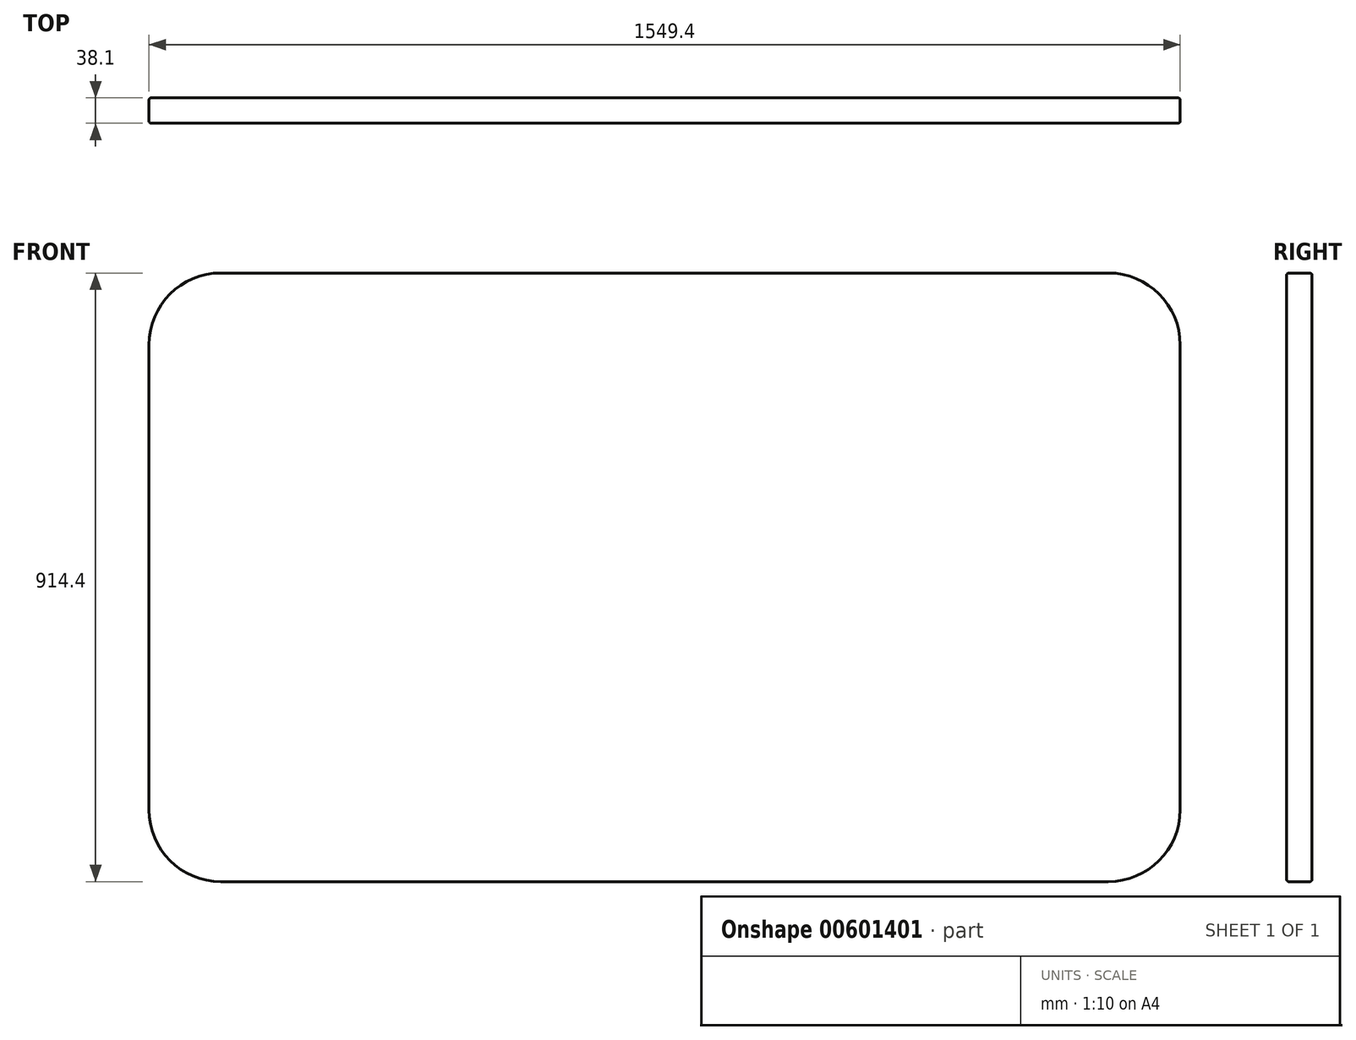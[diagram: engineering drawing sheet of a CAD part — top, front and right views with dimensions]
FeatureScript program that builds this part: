
annotation { "Feature Type Name" : "Feature", "Feature Type Description" : "" }
export const myFeature = defineFeature(function(context is Context, id is Id, definition is map)
    precondition{}
    {
        {
            var Q0;
            Q0=qCreatedBy(makeId("Front.planeOp"),FACE);
            var sketch = newSketch(context, id + "F0", { "sketchPlane" : qUnion([Q0])});
            skLineSegment(sketch, "E0.bottom", {"start": v(-666.75, 457.2) * mm, "end": v(666.75, 457.2) * mm});
            skLineSegment(sketch, "E0.top", {"start": v(-666.75, -457.2) * mm, "end": v(666.75, -457.2) * mm});
            skLineSegment(sketch, "E0.left", {"start": v(-774.7, 349.25) * mm, "end": v(-774.7, -349.25) * mm});
            skLineSegment(sketch, "E0.right", {"start": v(774.7, 349.25) * mm, "end": v(774.7, -349.25) * mm});
            skPoint(sketch, "E0.middle", {"position": v(0, 0) * mm});
            skPoint(sketch, "E1.visualSharp", {"position": v(774.7, 457.2) * mm});
            skArc(sketch, "E1.filletArc", {"start": v(774.7, 349.25) * mm, "mid": v(743.08, 425.58) * mm, "end": v(666.75, 457.2) * mm});
            skPoint(sketch, "E2.visualSharp", {"position": v(774.7, -457.2) * mm});
            skArc(sketch, "E2.filletArc", {"start": v(666.75, -457.2) * mm, "mid": v(743.08, -425.58) * mm, "end": v(774.7, -349.25) * mm});
            skPoint(sketch, "E3.visualSharp", {"position": v(-774.7, -457.2) * mm});
            skArc(sketch, "E3.filletArc", {"start": v(-774.7, -349.25) * mm, "mid": v(-743.08, -425.58) * mm, "end": v(-666.75, -457.2) * mm});
            skPoint(sketch, "E4.visualSharp", {"position": v(-774.7, 457.2) * mm});
            skArc(sketch, "E4.filletArc", {"start": v(-666.75, 457.2) * mm, "mid": v(-743.08, 425.58) * mm, "end": v(-774.7, 349.25) * mm});
            skSolve(sketch);
        }
        {
            var Q0;
            Q0 = qSketchRegion(id + "F0", true);
            extrude(context, id + "F1", {"entities" : qUnion([Q0]), "endBound" : BoundingType.SYMMETRIC, "depth" : 38.1 * mm, "offsetDistance" : 25.4 * mm});
        }
        {
            var Q0;
            Q0=makeQuery(id+"F1.opExtrude","CAP_EDGE",EDGE,{"disambiguationData":[OSD([sQuery(id+"F0.wireOp",EDGE,"E0.bottom")])],"isStart":false});
            var Q1;
            Q1=makeQuery(id+"F1.opExtrude","CAP_EDGE",EDGE,{"disambiguationData":[OSD([sQuery(id+"F0.wireOp",EDGE,"E4.filletArc")])],"isStart":false});
            var Q2;
            Q2=makeQuery(id+"F1.opExtrude","CAP_FACE",FACE,{"disambiguationData":[OSD([sQuery(id+"F0.wireOp",EDGE,"E0.bottom"),sQuery(id+"F0.wireOp",EDGE,"E0.top"),sQuery(id+"F0.wireOp",EDGE,"E0.left"),sQuery(id+"F0.wireOp",EDGE,"E0.right"),sQuery(id+"F0.wireOp",EDGE,"E1.filletArc"),sQuery(id+"F0.wireOp",EDGE,"E2.filletArc"),sQuery(id+"F0.wireOp",EDGE,"E3.filletArc"),sQuery(id+"F0.wireOp",EDGE,"E4.filletArc")])],"isStart":false});
            var Q3;
            Q3=makeQuery(id+"F1.opExtrude","CAP_EDGE",EDGE,{"disambiguationData":[OSD([sQuery(id+"F0.wireOp",EDGE,"E1.filletArc")])],"isStart":false});
            var Q4;
            Q4=makeQuery(id+"F1.opExtrude","CAP_FACE",FACE,{"disambiguationData":[OSD([sQuery(id+"F0.wireOp",EDGE,"E0.bottom"),sQuery(id+"F0.wireOp",EDGE,"E0.top"),sQuery(id+"F0.wireOp",EDGE,"E0.left"),sQuery(id+"F0.wireOp",EDGE,"E0.right"),sQuery(id+"F0.wireOp",EDGE,"E1.filletArc"),sQuery(id+"F0.wireOp",EDGE,"E2.filletArc"),sQuery(id+"F0.wireOp",EDGE,"E3.filletArc"),sQuery(id+"F0.wireOp",EDGE,"E4.filletArc")])],"isStart":true});
            var Q5;
            Q5=makeQuery(id+"F1.opExtrude","CAP_EDGE",EDGE,{"disambiguationData":[OSD([sQuery(id+"F0.wireOp",EDGE,"E2.filletArc")])],"isStart":true});
            fillet(context, id + "F2", {"entities" : qUnion([Q0, Q1, Q2, Q3, Q4, Q5]), "radius" : 3.35 * mm, "tangentPropagation" : true, "allowEdgeOverflow" : false});
        }
    });
